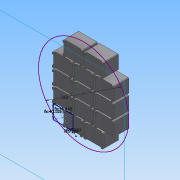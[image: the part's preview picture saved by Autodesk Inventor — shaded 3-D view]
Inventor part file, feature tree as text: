
AUTODESK INVENTOR PART (.ipt)
format: ipt  version: 2014 SP2 (Build 180246200, 246)  size: 1,051,648 bytes
history: native  units: mm
features: other x14, fillet x4, sketch x2, extrude x2, shell x2, mirror x2, pattern_linear x1, move_body x1
ambient origin geometry x8: Origin, YZ Plane, XZ Plane, XY Plane, X Axis, Y Axis, Z Axis, Center Point
bodies: Solid1 (feature_tree), Solid2 (feature_tree), Solid3 (feature_tree), Solid4 (feature_tree), Solid5 (feature_tree), Solid6 (feature_tree), Solid7 (feature_tree), Solid8 (feature_tree), Solid9 (feature_tree), Solid10 (feature_tree), Solid11 (feature_tree), Solid12 (feature_tree), Solid13 (feature_tree), Solid14 (feature_tree), Solid15 (feature_tree)
feature tree (28):
  sketch  "Sketch1"  dims[d0=56.4282mm d1=40.1051mm d2=40.9mm d3=0.0mm]
  extrude  "base"  Depth=40.1051mm
  shell  "Shell1"  Thickness=40.9mm
  extrude  "foot"  Depth=30.0mm
  mirror  "Mirror1"
  mirror  "Mirror2"
  shell  "Shell2"  Thickness=7.567mm
  fillet  "Fillet1"  Radius=3.32948mm
  fillet  "Fillet3"  Radius=1.8mm
  fillet  "Fillet5"  Radius=1.6mm
  fillet  "Fillet4"  Radius=2.0mm
  pattern_linear  "Rectangular Pattern1"  Spacing1=1.0mm  [1 undecoded]
  move_body  "Move Body1"
  sketch  "Sketch2"  dims[d4=19.0mm d5=7.567mm d6=7.567mm d7=3.32948mm d8=0.0mm d9=1.8mm d10=1.6mm d12=2.0mm d14=1.0mm d15=1.0mm d16=2.0mm d17=30.0mm d19=60.0mm d20=50.0mm d22=44.0mm d23=30.0mm d24=0.0mm d25=0.0mm d26=260.0mm]
  other  "Pattern of Solid1:1"
  other  "Pattern of Solid1:2"
  other  "Pattern of Solid1:3"
  other  "Pattern of Solid1:4"
  other  "Pattern of Solid1:5"
  other  "Pattern of Solid1:6"
  other  "Pattern of Solid1:7"
  other  "Pattern of Solid1:8"
  other  "Pattern of Solid1:9"
  other  "Pattern of Solid1:10"
  other  "Pattern of Solid1:11"
  other  "Pattern of Solid1:12"
  other  "Pattern of Solid1:13"
  other  "Pattern of Solid1:14"
note: 1 required parameter value undecoded (feature->parameter linkage not recoverable at this tier; creation-order binding heuristic only, values carry confidence <= 0.55)
